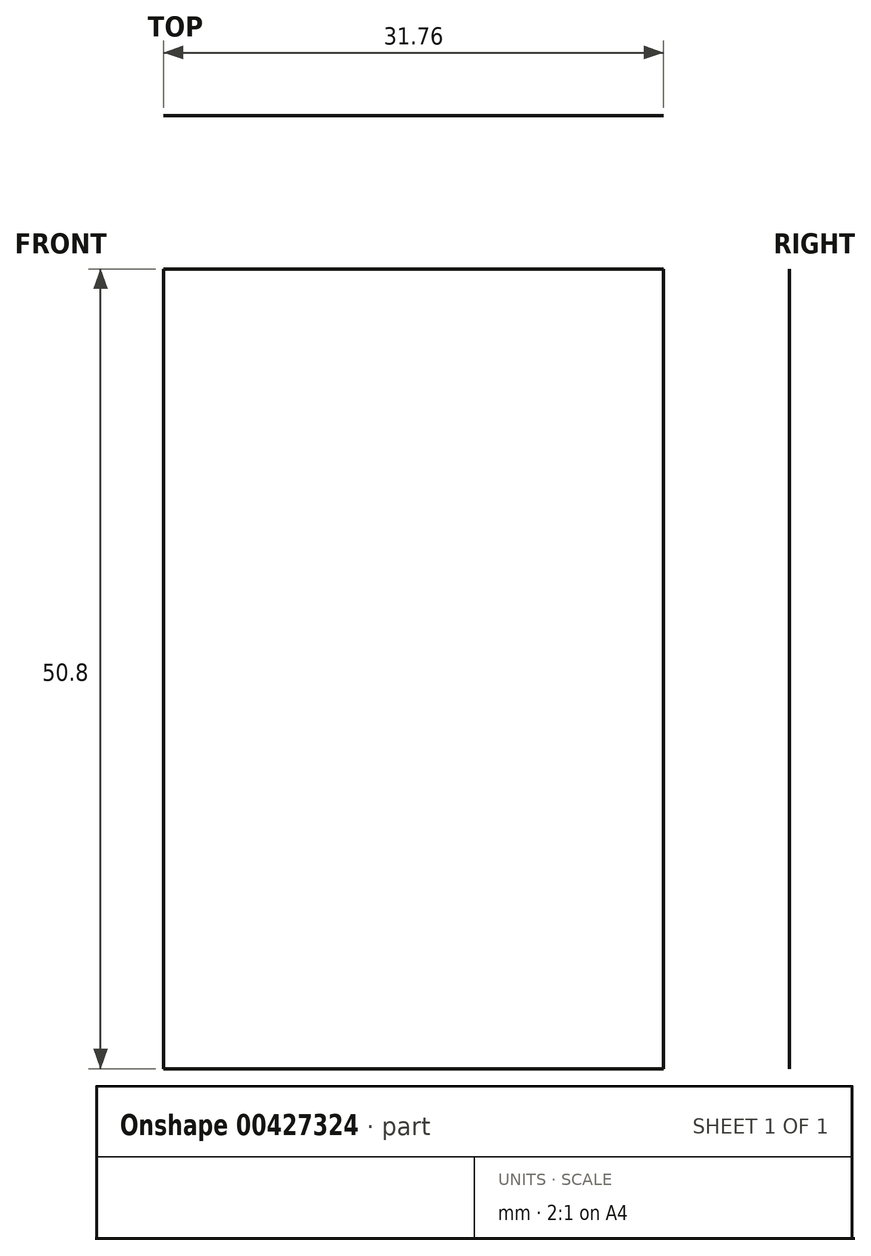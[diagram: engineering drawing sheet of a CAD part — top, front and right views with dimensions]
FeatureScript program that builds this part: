
annotation { "Feature Type Name" : "Feature", "Feature Type Description" : "" }
export const myFeature = defineFeature(function(context is Context, id is Id, definition is map)
    precondition{}
    {
        {
            var Q0;
            Q0=qCreatedBy(makeId("Front.planeOp"),FACE);
            var sketch = newSketch(context, id + "F0", { "sketchPlane" : qUnion([Q0])});
            skLineSegment(sketch, "E0.bottom", {"start": v(15.88, -25.4) * mm, "end": v(-15.88, -25.4) * mm});
            skLineSegment(sketch, "E0.top", {"start": v(15.88, 25.4) * mm, "end": v(-15.88, 25.4) * mm});
            skLineSegment(sketch, "E0.left", {"start": v(15.88, -25.4) * mm, "end": v(15.88, 25.4) * mm});
            skLineSegment(sketch, "E0.right", {"start": v(-15.88, -25.4) * mm, "end": v(-15.88, 25.4) * mm});
            skPoint(sketch, "E0.middle", {"position": v(0, 0) * mm});
            skSolve(sketch);
        }
        {
            var Q0;
            Q0 = qSketchRegion(id + "F0", true);
            extrude(context, id + "F1", {"entities" : qUnion([Q0]), "depth" : 1 / 812.8 * mm});
        }
    });
